FCSTD DOCUMENT  (FreeCAD 0.18R4 (GitTag))
Label: проэкт манипулятора
License: All rights reserved
LicenseURL: http://en.wikipedia.org/wiki/All_rights_reserved
objects: Sketcher::SketchObject×1, PartDesign::Body×1
note: 2 computed .brp shape members not serialized (recipe doc carries the construction recipe); baked Part::Feature solids carry a one-line shape summary decoded from their .brp

FEATURE [Sketcher::SketchObject] Sketch
  MapMode = 5
  Support = -> [XY_Plane]
  sketch-geometry (8):
    g0: LineSegment StartX=-15 StartY=0 StartZ=0 EndX=30 EndY=0 EndZ=0
    g1: LineSegment StartX=-15 StartY=20 StartZ=0 EndX=-15 EndY=0 EndZ=0
    g2: LineSegment StartX=-79.17 StartY=22.9381 StartZ=0 EndX=-79.17 EndY=13.7881 EndZ=0
    g3: LineSegment StartX=-79.17 StartY=13.7881 StartZ=0 EndX=-94.01 EndY=13.7881 EndZ=0
    g4: LineSegment StartX=-79.17 StartY=13.7881 StartZ=0 EndX=-0.229048 EndY=21.4299 EndZ=0
    g5: LineSegment StartX=-15 StartY=29.15 StartZ=0 EndX=-79.17 EndY=22.9381 EndZ=0
    g6: LineSegment StartX=-0.229048 StartY=21.4299 StartZ=0 EndX=-0.241336 EndY=2.6799 EndZ=0
    g7: LineSegment StartX=-15 StartY=29.15 StartZ=0 EndX=-15 EndY=20 EndZ=0
  constraints (23):
    c: Coincident(g0,g1)
    c: Parallel(g0,g-1)
    c: PointOnObject(g0,g-1)
    c: Coincident(g2,g3)
    c: Distance(g3) = 14.84
    c: Distance(g1) = 20
    c: Distance(g0) = 45
    c: Distance(g2) = 9.15
    c: DistanceX(g-1,g0) = 30
    c: Angle(g2,g3) = 1.5708
    c: Coincident(g2,g5)
    c: Coincident(g2,g4)
    c: PointOnObject(g1,g4)
    c: Coincident(g4,g6)
    c: Distance(g6,g0) = 15
    c: Coincident(g1,g7)
    c: Coincident(g5,g7)
    c: Distance(g5) = 64.47
    c: Distance(g7) = 9.15
    c: Parallel(g7,g1)
    c: Distance(g4) = 79.31
    c: Distance(g6) = 18.75
    c: Distance(g1,g4) = 14.84
FEATURE [PartDesign::Body] Body
  Group = -> [Sketch]
  Origin = -> Origin
